# Revit family: FPL4-EQ0622xWSxMPSx
name_source: partatom
category: Leuchten
units: mm (PartAtom-declared; Revit-internal decimal feet)

## family parameters
Basisbauteil = Fläche
Beim Laden mit Abzugskörper schneiden = Nein
Bemaßung runder Anschluss = Durchmesser verwenden
Gemeinsam genutzt = Nein
Lichtquelle = Ja
OmniClass-Nummer = 23.80.70.11
OmniClass-Titel = Luminaries for Internal Lighting
Raumberechnungspunkt = Nein
Teiletyp = Normal

## types (6) — shared parameters
Baugruppenkennzeichen = D5020200
Datei für fotometrisches Netz = Master_FPL4_MPS.IES
Emissionsform beim Rendern sichtbar = Nein
Farbfilter = 16777215
Farbtemperaturverschiebung bei Dämpfen der Lampe = <Keine Auswahl>
Hersteller = RIDI Leuchten GmbH
Lampe = LED
Neigungswinkel = 90.00°
Scheinlast = 33 VA
URL = www.ridi.de
Von Breite des Rechtecks ausssenden = 591 mm  [stored 1.93898 ft]
Von Länge des Rechtecks aussenden = 591 mm  [stored 1.93898 ft]
brand = RIDI
conformity mark = CE
electrical safety class = 2
height = 28 mm  [stored 0.0918635 ft]
ingress protection (IP) code = IP20/IP44
length = 622 mm  [stored 2.04068 ft]
nominal frequency = 50-60Hz
nominal voltage = 230
rated input power = 33
voltage type (AC, DC, UC) = AC
weight = 2,5 kg
width = 622 mm  [stored 2.04068 ft]
zero-valued in all types: Vorgabe-Ansicht

## per-type parameters (varying)
| type | Modell |
| FPL4-EQ0622FLWS840MPS0500 | 0823019 |
| FPL4-EQ0622FLWS830840MPS0500 | 0823020 |
| FPL4-EQ0622FLWS850865MPS0500 | 0823021 |
| FPL4-EQ0622DAWS840MPS0500 | 0833019 |
| FPL4-EQ0622DAWS830840MPS0500 | 0833020 |
| FPL4-EQ0622DAWS850865MPS0500 | 0833021 |

note: column(s) folded — value = type name in every type: product name

note: [stored X ft] marks values corroborated as IEEE doubles in the binary element streams (Revit-internal decimal feet)
